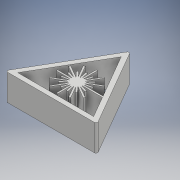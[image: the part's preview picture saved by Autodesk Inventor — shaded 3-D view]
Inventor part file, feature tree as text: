
AUTODESK INVENTOR PART (.ipt)
format: ipt  version: 2017 (Build 210142000, 142)  size: 316,928 bytes
history: native  units: mm
features: extrude x1, sketch x1, other x1
ambient origin geometry x8: Origin, YZ Plane, XZ Plane, XY Plane, X Axis, Y Axis, Z Axis, Center Point
bodies: Body1 (feature_tree)
feature tree (3):
  extrude  "Extrusion3"  Depth=3.0mm
  sketch  "Esquisse3"
  other  "Image2"
